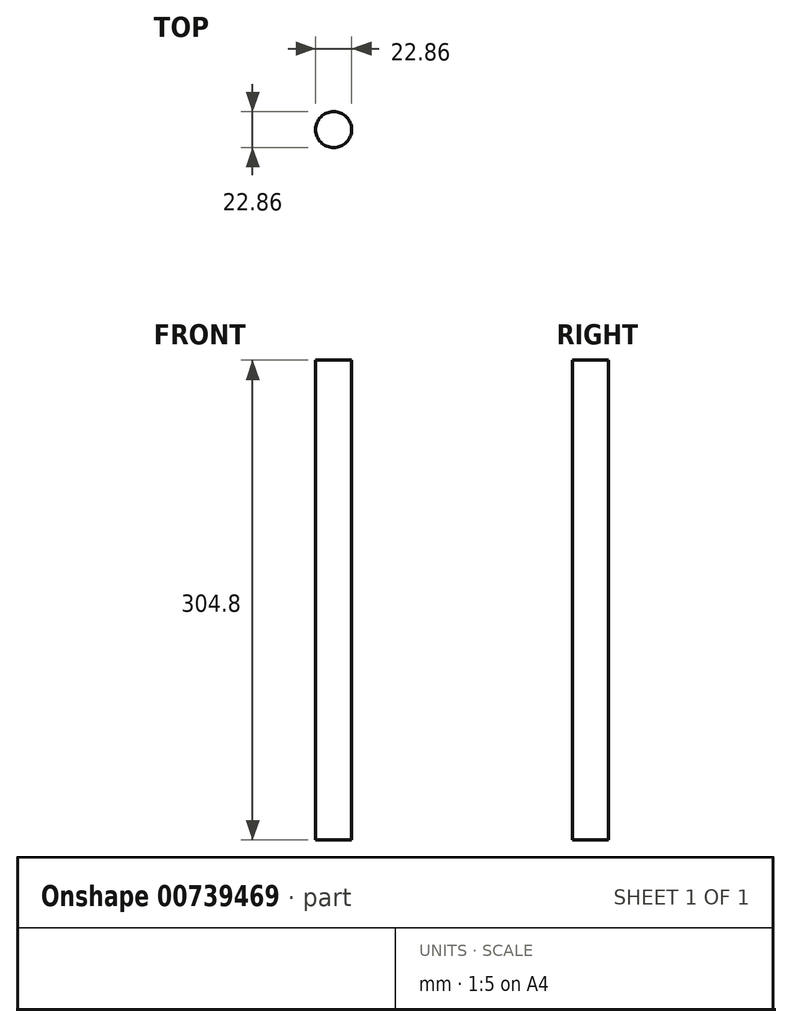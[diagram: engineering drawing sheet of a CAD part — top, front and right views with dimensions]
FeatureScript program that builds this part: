
annotation { "Feature Type Name" : "Feature", "Feature Type Description" : "" }
export const myFeature = defineFeature(function(context is Context, id is Id, definition is map)
    precondition{}
    {
        {
            var Q0;
            Q0=qCreatedBy(makeId("Top.planeOp"),FACE);
            var sketch = newSketch(context, id + "F0", { "sketchPlane" : qUnion([Q0])});
            skCircle(sketch, "E0", {"center": v(0, 0) * mm, "radius": 11.43 * mm});
            skSolve(sketch);
        }
        {
            var Q0;
            Q0=makeQuery(id+"F0.imprint","IMPRINT",FACE,{"disambiguationData":[TD([[makeQuery(id+"F0.imprint","IMPRINT",EDGE,{"derivedFrom":sQuery(id+"F0.wireOp",EDGE,"E0")}),1.0]])]});
            extrude(context, id + "F1", {"entities" : qUnion([Q0]), "depth" : 304.8 * mm, "offsetDistance" : 25.4 * mm});
        }
    });
